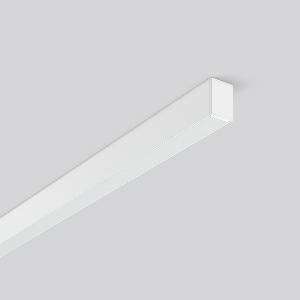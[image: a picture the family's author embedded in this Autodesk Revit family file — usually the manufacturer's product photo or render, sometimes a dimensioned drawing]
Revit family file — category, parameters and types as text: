
# Revit family: less_is_more_27_312199_002_76_cee0
name_source: partatom
category: Lighting Fixtures
units: mm (PartAtom-declared; Revit-internal decimal feet)

## family parameters
Cut with Voids When Loaded = No
Host = Face
Light Source = No
Part Type = Normal
Room Calculation Point = No
Round Connector Dimension = Use Diameter
Shared = No

## types (1)
- LESS IS MORE 27 (1 x LED Modul 830, 2600 lm, 3000)
    Apparent Load = 34 VA
    CIE Flux Codes = 65 89 98 100 100
    Color Rendering = 80
    Color Temperature = 3000
    Default Elevation = 1800 mm
    Description = Series: LESS IS MORE 27
Ceiling luminaire with slim design. Housing: extruded aluminium profile, powder-coated. End cap aluminium powder-coated. Diffuser made of non-yellowing plastic (PMMA) microprismatic. Suitable for Ceiling mounting, Wall (surface). External driver with connecting cable. 
Colour: traffic white, matt (RAL 9016)
Length: 1212 mm
Width: 28 mm
Height: 38 mm
Lamp: LED
Socket: without socket
Colour temperature: 3000K
Colour rendering index (CRI): 82
System power: 34 W
Rated luminous flux: 2600 lm
Luminous efficiency: 76 lm/W
Control gear: Voltage converter, DALI dim.
Protection class: II
Type of protection: IP 20
    Height = 38 mm
    Lamp = 1 x LED Modul 830
    Lamp Light Flux = 2600 lm
    Lamp count = 1
    Length = 1212 mm
    Lifetime = 50000 h
    Luminous efficacy = 76 lm/W
    Manufacturer = RZB
    ModVariant = No
    Model = 312199.002.76
    Mounting Place = Ceiling, Wall
    Mounting Type = Surface mounted
    Number of Poles = 1
    OnlyDefault = Yes
    Power Factor = 1
    Product Name = LESS IS MORE 27
    Product group = Surface mounted LED linear luminaires
    ProductGroupID = 307
    Protection Class = Protection class II
    Protection Degree = IP 20
    RLX_Detail_Level = 1
    RLX_Emergency_Light_Flux = 0 lm
    RLX_Emergency_Type = 0
    RLX_Emergency_Type_DB = No
    RlxData = <blob elided: 24029 chars, md5=68993c32>
    Socket = socket
    Standby Power = 0 W
    System Light Flux = 2600 lm
    System Power = 34 W
    Type Comments = Product without accessories
    Type Image = 312196.002.jpg
    URL = http://relux.com
    VarID = ---
    Voltage = 230 V
    Voltage Range = 220-240 V
    Weight = 0.00 kg
    Width = 28 mm

## geometry (parser evidence)
native form markers: Blend x4, Sweep x11
no freeform markers — native parametric forms only
